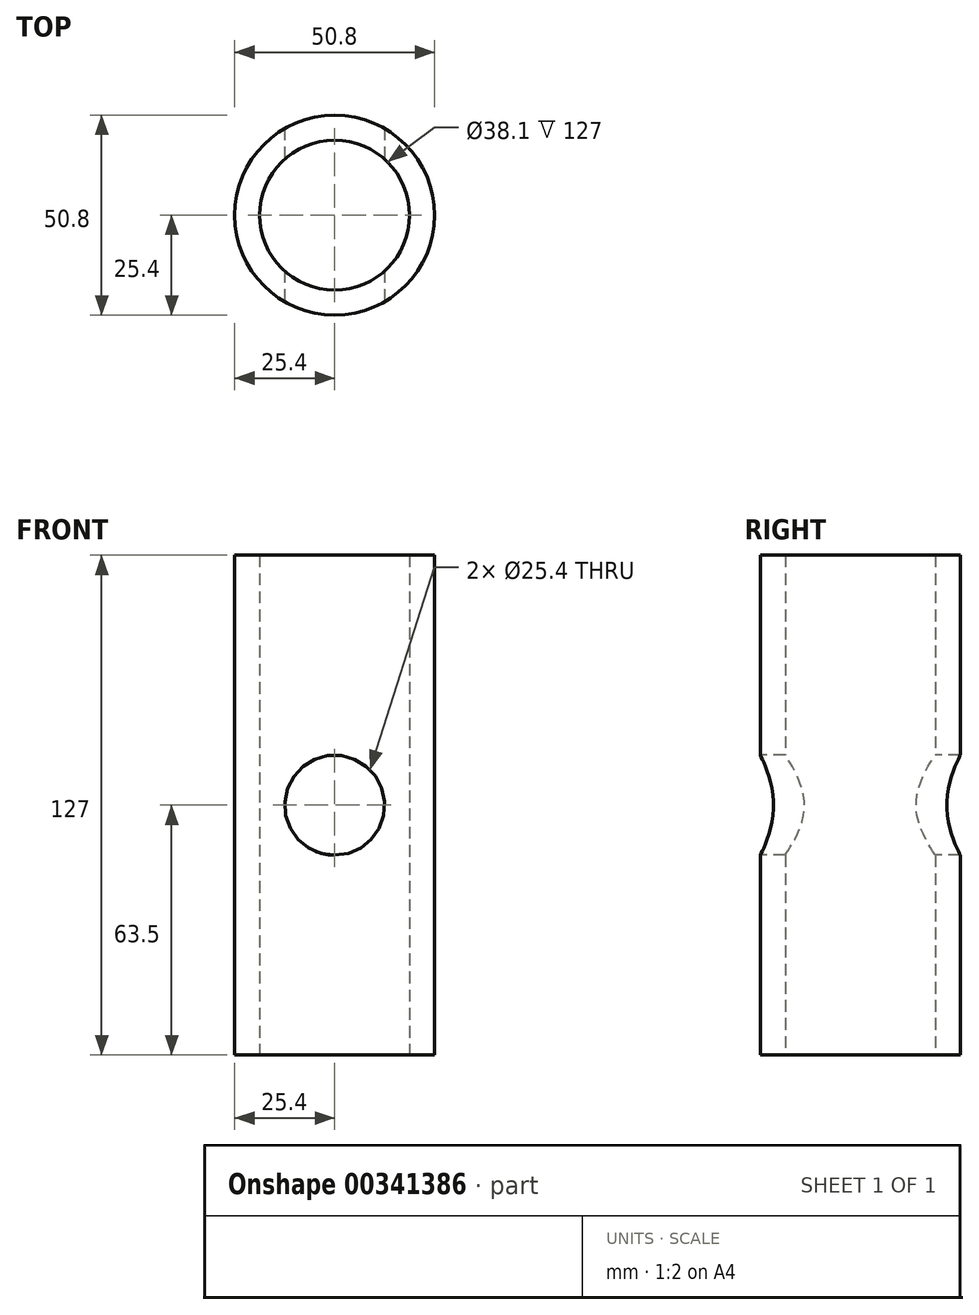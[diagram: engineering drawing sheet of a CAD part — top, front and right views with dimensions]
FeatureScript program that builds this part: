
annotation { "Feature Type Name" : "Feature", "Feature Type Description" : "" }
export const myFeature = defineFeature(function(context is Context, id is Id, definition is map)
    precondition{}
    {
        {
            var Q0;
            Q0=qCreatedBy(makeId("Top.planeOp"),FACE);
            var sketch = newSketch(context, id + "F0", { "sketchPlane" : qUnion([Q0])});
            skCircle(sketch, "E0", {"center": v(0, 0) * mm, "radius": 25.4 * mm});
            skCircle(sketch, "E1", {"center": v(0, 0) * mm, "radius": 19.05 * mm});
            skSolve(sketch);
        }
        {
            var Q0;
            Q0=makeQuery(id+"F0.imprint","IMPRINT",FACE,{"disambiguationData":[TD([[makeQuery(id+"F0.imprint","IMPRINT",EDGE,{"derivedFrom":sQuery(id+"F0.wireOp",EDGE,"E0")}),1.0]])]});
            var Q1;
            Q1=sQuery(id+"F0.wireOp",EDGE,"E0");
            var Q2;
            Q2=sQuery(id+"F0.wireOp",EDGE,"E1");
            extrude(context, id + "F1", {"entities" : qUnion([Q0]), "surfaceEntities" : qUnion([Q1, Q2]), "depth" : 127 * mm});
        }
        {
            var Q0;
            Q0=qCreatedBy(makeId("Front.planeOp"),FACE);
            cPlane(context, id + "F2", {"entities" : qUnion([Q0]), "cplaneType" : CPlaneType.OFFSET, "offset" : 25.4 * mm, "width" : 152.4 * mm, "height" : 152.4 * mm});
        }
        {
            var Q0;
            Q0=qCreatedBy(id+"F2.planeOp",FACE);
            var sketch = newSketch(context, id + "F3", { "sketchPlane" : qUnion([Q0])});
            skLineSegment(sketch, "E2", {"start": v(0, 0) * mm, "end": v(0, 63.5) * mm});
            skCircle(sketch, "E3", {"center": v(0, 63.5) * mm, "radius": 12.7 * mm});
            skSolve(sketch);
        }
        {
            var Q0;
            Q0=makeQuery(id+"F3.imprint","IMPRINT",FACE,{"disambiguationData":[TD([[makeQuery(id+"F3.imprint","IMPRINT",EDGE,{"derivedFrom":sQuery(id+"F3.wireOp",EDGE,"E3")}),1.0]])]});
            extrude(context, id + "F4", {"entities" : qUnion([Q0]), "operationType" : NewBodyOperationType.REMOVE, "oppositeDirection" : true, "depth" : 50.8 * mm});
        }
    });
